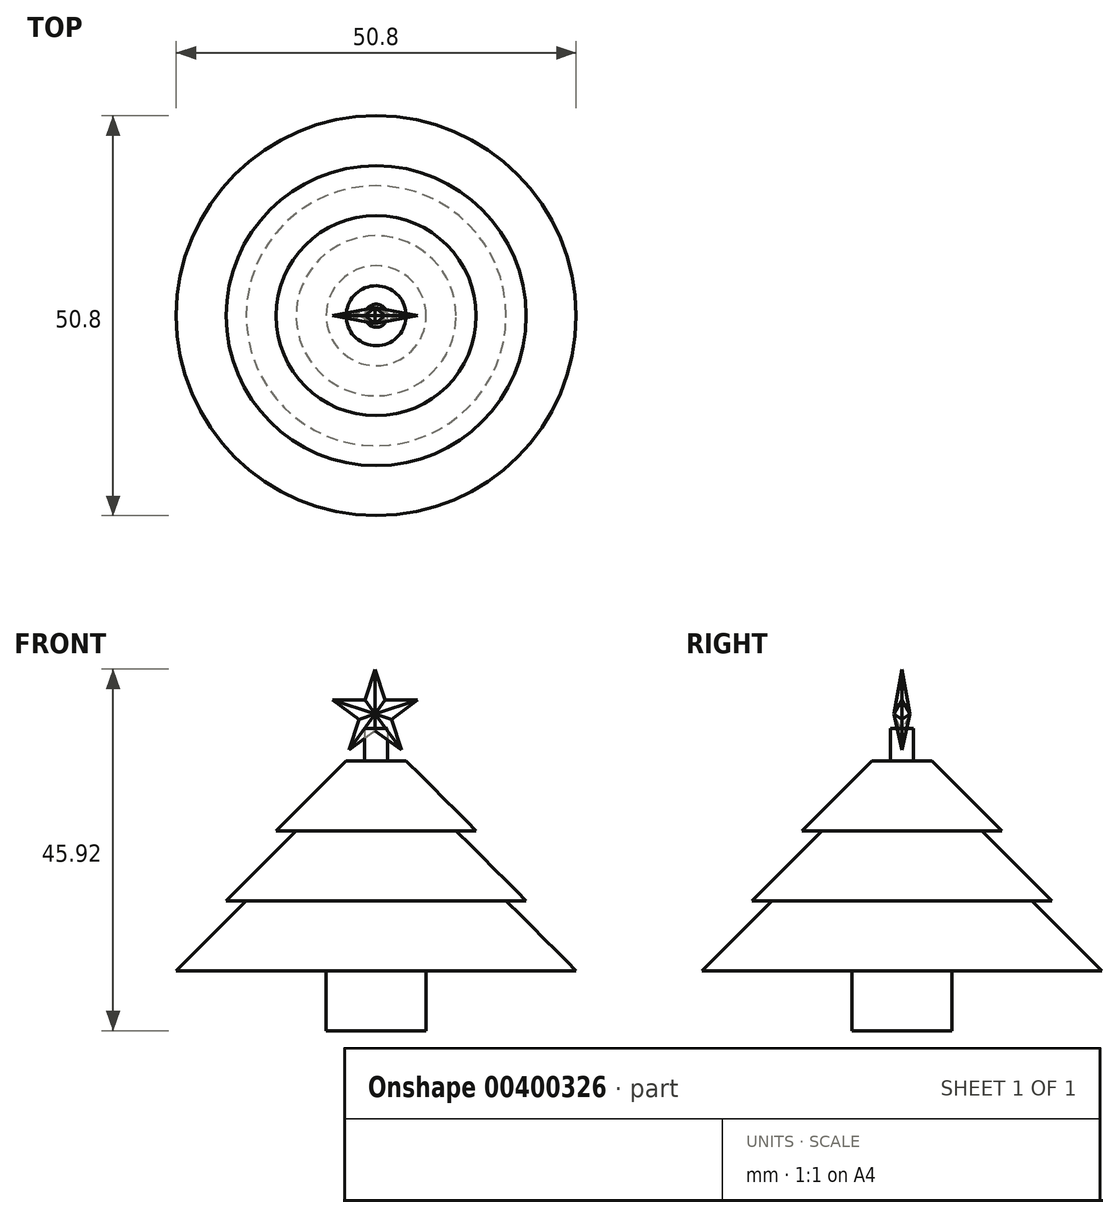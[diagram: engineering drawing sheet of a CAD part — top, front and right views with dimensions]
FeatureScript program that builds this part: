
annotation { "Feature Type Name" : "Feature", "Feature Type Description" : "" }
export const myFeature = defineFeature(function(context is Context, id is Id, definition is map)
    precondition{}
    {
        {
            var Q0;
            Q0=qCreatedBy(makeId("Top.planeOp"),FACE);
            var sketch = newSketch(context, id + "F0", { "sketchPlane" : qUnion([Q0])});
            skCircle(sketch, "E0", {"center": v(0, 0) * mm, "radius": 6.35 * mm});
            skSolve(sketch);
        }
        {
            var Q0;
            Q0=makeQuery(id+"F0.imprint","IMPRINT",FACE,{"disambiguationData":[TD([[makeQuery(id+"F0.imprint","IMPRINT",EDGE,{"derivedFrom":sQuery(id+"F0.wireOp",EDGE,"E0")}),1.0]])]});
            extrude(context, id + "F1", {"entities" : qUnion([Q0]), "depth" : 7.62 * mm});
        }
        {
            var Q0;
            Q0=makeQuery(id+"F1.opExtrude","CAP_FACE",FACE,{"disambiguationData":[OSD([sQuery(id+"F0.wireOp",EDGE,"E0")])],"isStart":false});
            var sketch = newSketch(context, id + "F2", { "sketchPlane" : qUnion([Q0])});
            skCircle(sketch, "E1", {"center": v(0, 0) * mm, "radius": 25.4 * mm});
            skSolve(sketch);
        }
        {
            var Q0;
            Q0 = qSketchRegion(id + "F2", true);
            extrude(context, id + "F3", {"entities" : qUnion([Q0]), "operationType" : NewBodyOperationType.ADD, "depth" : 8.9 * mm, "hasDraft" : true, "draftAngle" : 45 * degree, "draftPullDirection" : true});
        }
        {
            var Q0;
            Q0=makeQuery(id+"F3.opExtrude","CAP_FACE",FACE,{"disambiguationData":[OSD([sQuery(id+"F2.wireOp",EDGE,"E1")])],"isStart":false});
            var sketch = newSketch(context, id + "F4", { "sketchPlane" : qUnion([Q0])});
            skCircle(sketch, "E2", {"center": v(0, 0) * mm, "radius": 19.05 * mm});
            skSolve(sketch);
        }
        {
            var Q0;
            Q0=makeQuery(id+"F4.imprint","IMPRINT",FACE,{"disambiguationData":[TD([[makeQuery(id+"F4.imprint","IMPRINT",EDGE,{"derivedFrom":makeQuery(id+"F3.opExtrude","CAP_EDGE",EDGE,{"disambiguationData":[OSD([sQuery(id+"F2.wireOp",EDGE,"E1")])],"isStart":false})}),1.0]])]});
            var Q1;
            Q1=makeQuery(id+"F4.imprint","IMPRINT",FACE,{"disambiguationData":[TD([[makeQuery(id+"F4.imprint","IMPRINT",EDGE,{"derivedFrom":sQuery(id+"F4.wireOp",EDGE,"E2")}),1.0]])]});
            extrude(context, id + "F5", {"entities" : qUnion([Q0, Q1]), "operationType" : NewBodyOperationType.ADD, "depth" : 8.9 * mm, "hasDraft" : true, "draftAngle" : 45 * degree, "draftPullDirection" : true});
        }
        {
            var Q0;
            Q0=makeQuery(id+"F5.opExtrude","CAP_FACE",FACE,{"disambiguationData":[OSD([sQuery(id+"F4.wireOp",EDGE,"E2")])],"isStart":false});
            var sketch = newSketch(context, id + "F6", { "sketchPlane" : qUnion([Q0])});
            skCircle(sketch, "E3", {"center": v(0, 0) * mm, "radius": 12.7 * mm});
            skSolve(sketch);
        }
        {
            var Q0;
            Q0 = qSketchRegion(id + "F6", true);
            extrude(context, id + "F7", {"entities" : qUnion([Q0]), "operationType" : NewBodyOperationType.ADD, "depth" : 8.9 * mm, "hasDraft" : true, "draftAngle" : 45 * degree, "draftPullDirection" : true});
        }
        {
            var Q0;
            Q0=makeQuery(id+"F7.opExtrude","CAP_FACE",FACE,{"disambiguationData":[OSD([sQuery(id+"F6.wireOp",EDGE,"E3")])],"isStart":false});
            var sketch = newSketch(context, id + "F8", { "sketchPlane" : qUnion([Q0])});
            skCircle(sketch, "E4", {"center": v(0, 0) * mm, "radius": 1.47 * mm});
            skSolve(sketch);
        }
        {
            var Q0;
            Q0 = qSketchRegion(id + "F8", true);
            extrude(context, id + "F9", {"entities" : qUnion([Q0]), "operationType" : NewBodyOperationType.ADD, "depth" : 4.11 * mm});
        }
        {
            var Q0;
            Q0=qCreatedBy(makeId("Front.planeOp"),FACE);
            var sketch = newSketch(context, id + "F10", { "sketchPlane" : qUnion([Q0])});
            skPoint(sketch, "E5.0.midPoint", {"position": v(-40.9, 49.05) * mm});
            skPoint(sketch, "E5.cCircle.center.orphan", {"position": v(-40.9, 53.65) * mm});
            skLineSegment(sketch, "E6", {"start": v(-40.9, 59.33) * mm, "end": v(-42.17, 55.4) * mm});
            skLineSegment(sketch, "E7", {"start": v(-37.56, 49.05) * mm, "end": v(-38.83, 52.98) * mm});
            skLineSegment(sketch, "E8", {"start": v(-44.23, 49.05) * mm, "end": v(-40.9, 51.48) * mm});
            skLineSegment(sketch, "E9", {"start": v(-37.56, 49.05) * mm, "end": v(-40.9, 51.48) * mm});
            skLineSegment(sketch, "E10", {"start": v(-46.3, 55.4) * mm, "end": v(-42.17, 55.4) * mm});
            skLineSegment(sketch, "E11.trimOffspring", {"start": v(-42.96, 52.98) * mm, "end": v(-44.23, 49.05) * mm});
            skLineSegment(sketch, "E12.trimOffspring", {"start": v(-39.62, 55.4) * mm, "end": v(-35.5, 55.4) * mm});
            skLineSegment(sketch, "E13.trimOffspring", {"start": v(-39.62, 55.4) * mm, "end": v(-40.9, 59.33) * mm});
            skLineSegment(sketch, "E14.trimOffspring", {"start": v(-38.83, 52.98) * mm, "end": v(-35.5, 55.4) * mm});
            skLineSegment(sketch, "E15.trimOffspring", {"start": v(-42.96, 52.98) * mm, "end": v(-46.3, 55.4) * mm});
            skLineSegment(sketch, "E16", {"start": v(-40.9, 59.33) * mm, "end": v(-40.9, 53.65) * mm});
            skLineSegment(sketch, "E17", {"start": v(-39.62, 55.4) * mm, "end": v(-40.9, 53.65) * mm});
            skLineSegment(sketch, "E18", {"start": v(-40.9, 53.65) * mm, "end": v(-42.17, 55.4) * mm});
            skLineSegment(sketch, "E19", {"start": v(-46.3, 55.4) * mm, "end": v(-40.9, 53.65) * mm});
            skLineSegment(sketch, "E20", {"start": v(-42.96, 52.98) * mm, "end": v(-40.9, 53.65) * mm});
            skLineSegment(sketch, "E21", {"start": v(-44.23, 49.05) * mm, "end": v(-40.9, 53.65) * mm});
            skLineSegment(sketch, "E22", {"start": v(-40.9, 51.48) * mm, "end": v(-40.9, 53.65) * mm});
            skLineSegment(sketch, "E23", {"start": v(-37.56, 49.05) * mm, "end": v(-40.9, 53.65) * mm});
            skLineSegment(sketch, "E24", {"start": v(-38.83, 52.98) * mm, "end": v(-40.9, 53.65) * mm});
            skLineSegment(sketch, "E25", {"start": v(-35.5, 55.4) * mm, "end": v(-40.9, 53.65) * mm});
            skSolve(sketch);
        }
        {
            var Q0;
            Q0=makeQuery(id+"F10.imprint","IMPRINT",FACE,{"disambiguationData":[TD([[makeQuery(id+"F10.imprint","IMPRINT",EDGE,{"derivedFrom":sQuery(id+"F10.wireOp",EDGE,"E6")}),1.0]])]});
            var Q1;
            Q1=makeQuery(id+"F10.imprint","IMPRINT",FACE,{"disambiguationData":[TD([[makeQuery(id+"F10.imprint","IMPRINT",EDGE,{"derivedFrom":sQuery(id+"F10.wireOp",EDGE,"E13.trimOffspring")}),1.0]])]});
            var Q2;
            Q2=makeQuery(id+"F10.imprint","IMPRINT",FACE,{"disambiguationData":[TD([[makeQuery(id+"F10.imprint","IMPRINT",EDGE,{"derivedFrom":sQuery(id+"F10.wireOp",EDGE,"E12.trimOffspring")}),-1.0]])]});
            var Q3;
            Q3=makeQuery(id+"F10.imprint","IMPRINT",FACE,{"disambiguationData":[TD([[makeQuery(id+"F10.imprint","IMPRINT",EDGE,{"derivedFrom":sQuery(id+"F10.wireOp",EDGE,"E14.trimOffspring")}),1.0]])]});
            var Q4;
            Q4=makeQuery(id+"F10.imprint","IMPRINT",FACE,{"disambiguationData":[TD([[makeQuery(id+"F10.imprint","IMPRINT",EDGE,{"derivedFrom":sQuery(id+"F10.wireOp",EDGE,"E7")}),1.0]])]});
            var Q5;
            Q5=makeQuery(id+"F10.imprint","IMPRINT",FACE,{"disambiguationData":[TD([[makeQuery(id+"F10.imprint","IMPRINT",EDGE,{"derivedFrom":sQuery(id+"F10.wireOp",EDGE,"E9")}),-1.0]])]});
            var Q6;
            Q6=makeQuery(id+"F10.imprint","IMPRINT",FACE,{"disambiguationData":[TD([[makeQuery(id+"F10.imprint","IMPRINT",EDGE,{"derivedFrom":sQuery(id+"F10.wireOp",EDGE,"E8")}),1.0]])]});
            var Q7;
            Q7=makeQuery(id+"F10.imprint","IMPRINT",FACE,{"disambiguationData":[TD([[makeQuery(id+"F10.imprint","IMPRINT",EDGE,{"derivedFrom":sQuery(id+"F10.wireOp",EDGE,"E11.trimOffspring")}),1.0]])]});
            var Q8;
            Q8=makeQuery(id+"F10.imprint","IMPRINT",FACE,{"disambiguationData":[TD([[makeQuery(id+"F10.imprint","IMPRINT",EDGE,{"derivedFrom":sQuery(id+"F10.wireOp",EDGE,"E15.trimOffspring")}),-1.0]])]});
            var Q9;
            Q9=makeQuery(id+"F10.imprint","IMPRINT",FACE,{"disambiguationData":[TD([[makeQuery(id+"F10.imprint","IMPRINT",EDGE,{"derivedFrom":sQuery(id+"F10.wireOp",EDGE,"E10")}),-1.0]])]});
            extrude(context, id + "F11", {"entities" : qUnion([Q0, Q1, Q2, Q3, Q4, Q5, Q6, Q7, Q8, Q9]), "depth" : 25.4 * mm, "hasDraft" : true, "draftAngle" : 60 * degree, "draftPullDirection" : true, "hasSecondDirection" : true, "secondDirectionOppositeDirection" : true, "secondDirectionDepth" : 25.4 * mm, "hasSecondDirectionDraft" : true, "secondDirectionDraftAngle" : 60 * degree, "secondDirectionDraftPullDirection" : true});
        }
        {
            var Q0;
            Q0=makeQuery(id+"F11.*.split.splitOp","SPLIT",BODY,{"derivedFrom":makeQuery(id+"F11.opExtrude","SWEPT_BODY",BODY,{"disambiguationData":[OSD([sQuery(id+"F10.wireOp",EDGE,"E6"),sQuery(id+"F10.wireOp",EDGE,"E7"),sQuery(id+"F10.wireOp",EDGE,"E8"),sQuery(id+"F10.wireOp",EDGE,"E9"),sQuery(id+"F10.wireOp",EDGE,"E10"),sQuery(id+"F10.wireOp",EDGE,"E11.trimOffspring"),sQuery(id+"F10.wireOp",EDGE,"E12.trimOffspring"),sQuery(id+"F10.wireOp",EDGE,"E13.trimOffspring"),sQuery(id+"F10.wireOp",EDGE,"E14.trimOffspring"),sQuery(id+"F10.wireOp",EDGE,"E15.trimOffspring")])]})});
            transform(context, id + "F12", {"entities" : qUnion([Q0]), "transformType" : TransformType.TRANSLATION_3D, "dx" : 40.77 * mm, "dy" : 0 * mm, "dz" : -13.4 * mm, "makeCopy" : false});
        }
    });
